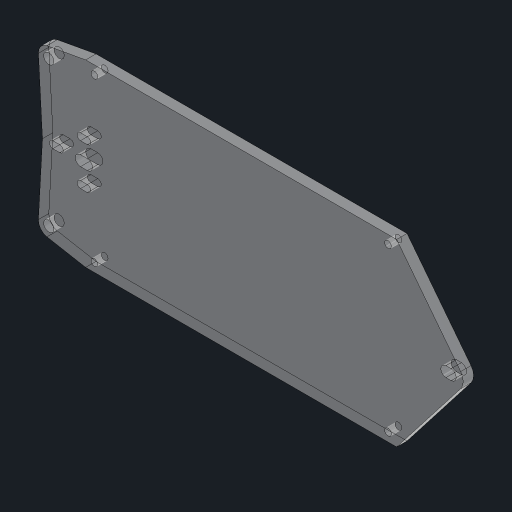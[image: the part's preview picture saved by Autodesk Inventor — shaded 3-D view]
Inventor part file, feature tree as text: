
AUTODESK INVENTOR PART (.ipt)
format: ipt  version: 2023.2 (Build 272271030, 271C)  size: 478,720 bytes
history: native  units: mm
features: extrude x2, fillet x2, mirror x2, sketch x2, projected_geometry x1
ambient origin geometry x8: Origin, YZ Plane, XZ Plane, XY Plane, X Axis, Y Axis, Z Axis, Center Point
bodies: Solid1 (feature_tree)
feature tree (9):
  extrude  "Extrusion1"  Depth=42.0mm
  extrude  "Extrusion6"  Depth=0.5mm
  fillet  "Fillet4"  Radius=36.0mm
  mirror  "Mirror3"
  mirror  "Mirror4"
  fillet  "Fillet5"  Radius=127.0mm
  sketch  "Sketch1"  dims[d0=90.0mm d1=42.0mm]
  sketch  "Sketch6"  dims[d2=5.0mm d3=22.0mm d5=36.0mm d6=127.0mm d7=8.0mm d8=8.0mm d9=0.0mm d10=3.0mm d11=3.0mm d12=8.0mm d13=3.0mm d14=1.5mm d15=8.5mm d16=1.25mm d17=5.0mm d18=5.0mm d19=1.0mm d20=3.0mm d21=16.0mm d22=12.0mm d23=1.0mm d24=1.0mm d25=1.0mm d26=2.0mm d27=1.0mm d28=2.0mm d29=2.0mm d30=2.0mm d31=2.0mm d32=2.0mm d33=2.0mm d34=5.0mm d35=5.0mm d36=5.0mm d37=1.5mm d38=1.5mm d39=3.0mm d40=0.0mm d102=2.0mm d103=2.5mm d104=2.5mm d105=2.5mm d106=2.5mm d111=3.0mm d113=5.0mm d114=3.0mm d115=5.0mm d116=2.0mm d117=2.0mm d118=2.0mm d119=2.0mm d120=6.2mm d121=3.0mm d122=3.0mm d123=3.0mm d124=3.0mm d125=1.5mm d126=3.0mm d127=3.0mm d128=38.971143mm d129=2.0mm d130=0.0mm d131=30.0mm d133=38.971143mm d134=10.0mm d136=10.0mm d138=3.1mm d139=3.1mm d140=0.872665mm d141=0.5mm d142=0.872665mm]
  projected_geometry  "Projected Loop6"
